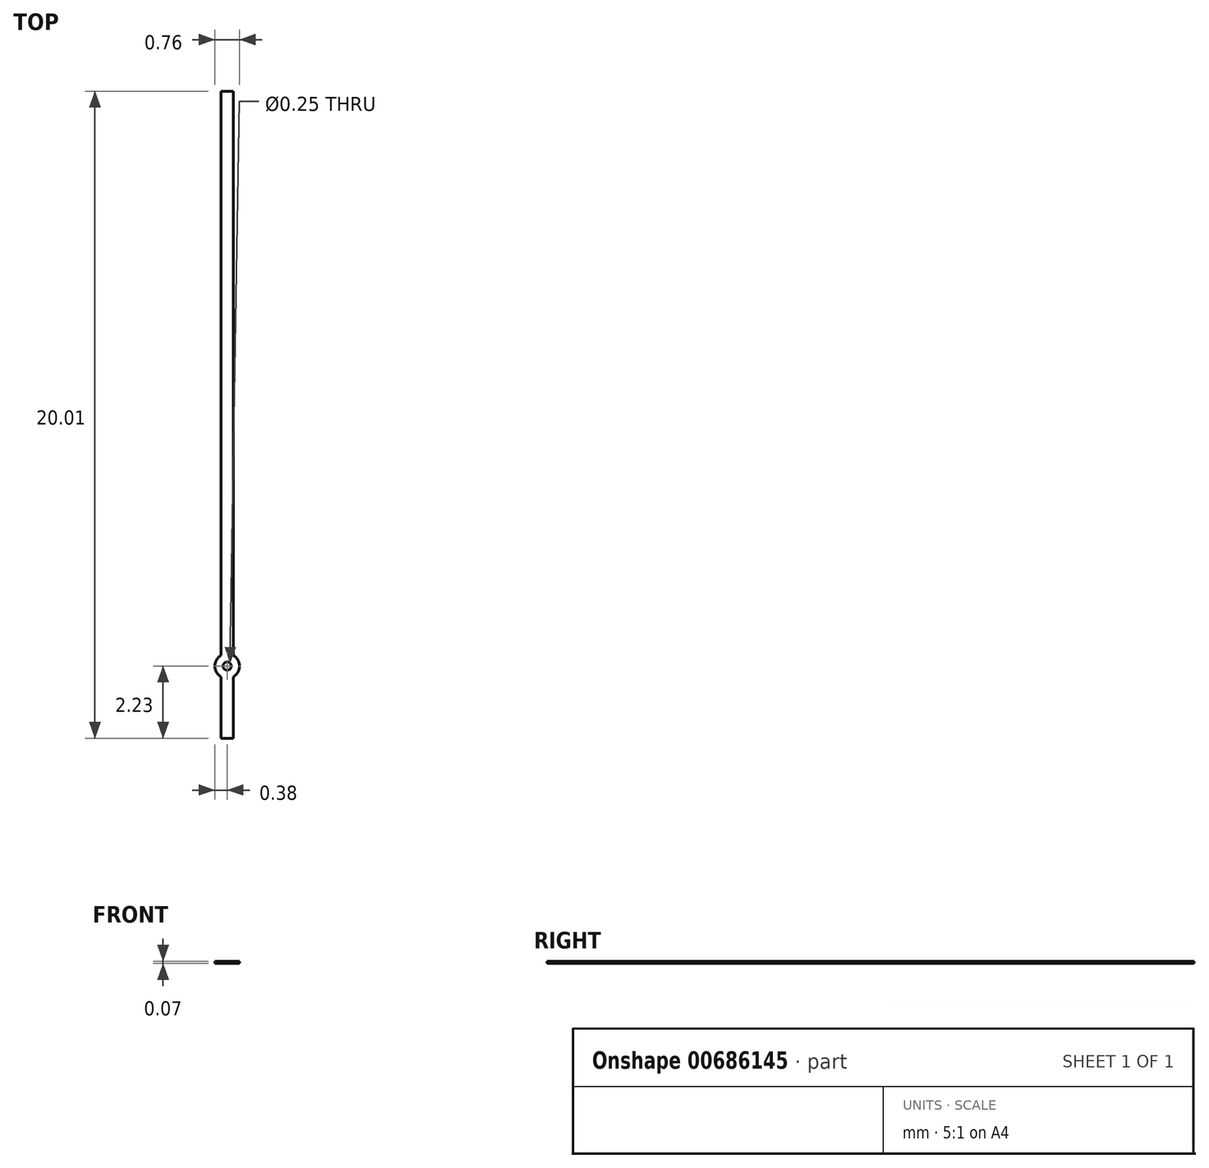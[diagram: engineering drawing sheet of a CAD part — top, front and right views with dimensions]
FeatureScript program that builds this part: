
annotation { "Feature Type Name" : "Feature", "Feature Type Description" : "" }
export const myFeature = defineFeature(function(context is Context, id is Id, definition is map)
    precondition{}
    {
        {
            var Q0;
            Q0=qCreatedBy(makeId("Top.planeOp"),FACE);
            var sketch = newSketch(context, id + "F0", { "sketchPlane" : qUnion([Q0])});
            skArc(sketch, "E0", {"start": v(-0.2, 0.33) * mm, "mid": v(-0.38, 0) * mm, "end": v(-0.2, -0.33) * mm});
            skLineSegment(sketch, "E1", {"start": v(0.2, 0.33) * mm, "end": v(0.2, 17.78) * mm});
            skLineSegment(sketch, "E2", {"start": v(0.2, 17.78) * mm, "end": v(0, 17.78) * mm});
            skLineSegment(sketch, "E3.MirrorCS", {"start": v(-0.2, 0.33) * mm, "end": v(-0.2, 17.78) * mm});
            skLineSegment(sketch, "E4.MirrorCS", {"start": v(-0.2, 17.78) * mm, "end": v(0, 17.78) * mm});
            skLineSegment(sketch, "E5", {"start": v(0.2, -0.33) * mm, "end": v(0.2, -2.23) * mm});
            skLineSegment(sketch, "E6", {"start": v(0.2, -2.23) * mm, "end": v(0, -2.23) * mm});
            skLineSegment(sketch, "E7.MirrorCS", {"start": v(-0.2, -2.23) * mm, "end": v(0, -2.23) * mm});
            skLineSegment(sketch, "E8.MirrorCS", {"start": v(-0.2, -0.33) * mm, "end": v(-0.2, -2.23) * mm});
            skArc(sketch, "E9.trimOffspring", {"start": v(0.2, -0.33) * mm, "mid": v(0.38, 0) * mm, "end": v(0.2, 0.33) * mm});
            skSolve(sketch);
        }
        {
            var Q0;
            Q0=makeQuery(id+"F0.imprint","IMPRINT",FACE,{"disambiguationData":[TD([[makeQuery(id+"F0.imprint","IMPRINT",EDGE,{"derivedFrom":sQuery(id+"F0.wireOp",EDGE,"E0")}),1.0]])]});
            extrude(context, id + "F1", {"entities" : qUnion([Q0]), "depth" : 0.07 * mm, "offsetDistance" : 25.4 * mm});
        }
        {
            var Q0;
            Q0=makeQuery(id+"F1.opExtrude","CAP_FACE",FACE,{"disambiguationData":[OSD([sQuery(id+"F0.wireOp",EDGE,"E0"),sQuery(id+"F0.wireOp",EDGE,"E1"),sQuery(id+"F0.wireOp",EDGE,"E2"),sQuery(id+"F0.wireOp",EDGE,"E3.MirrorCS"),sQuery(id+"F0.wireOp",EDGE,"E4.MirrorCS"),sQuery(id+"F0.wireOp",EDGE,"E5"),sQuery(id+"F0.wireOp",EDGE,"E6"),sQuery(id+"F0.wireOp",EDGE,"E7.MirrorCS"),sQuery(id+"F0.wireOp",EDGE,"E8.MirrorCS"),sQuery(id+"F0.wireOp",EDGE,"E9.trimOffspring")])],"isStart":false});
            var sketch = newSketch(context, id + "F2", { "sketchPlane" : qUnion([Q0])});
            skCircle(sketch, "E10", {"center": v(0, 0) * mm, "radius": 0.13 * mm});
            skSolve(sketch);
        }
        {
            var Q0;
            Q0=makeQuery(id+"F2.imprint","IMPRINT",FACE,{"disambiguationData":[TD([[makeQuery(id+"F2.imprint","IMPRINT",EDGE,{"derivedFrom":sQuery(id+"F2.wireOp",EDGE,"E10")}),1.0]])]});
            extrude(context, id + "F3", {"entities" : qUnion([Q0]), "operationType" : NewBodyOperationType.REMOVE, "oppositeDirection" : true, "depth" : 25.4 * mm, "offsetDistance" : 25.4 * mm});
        }
    });
